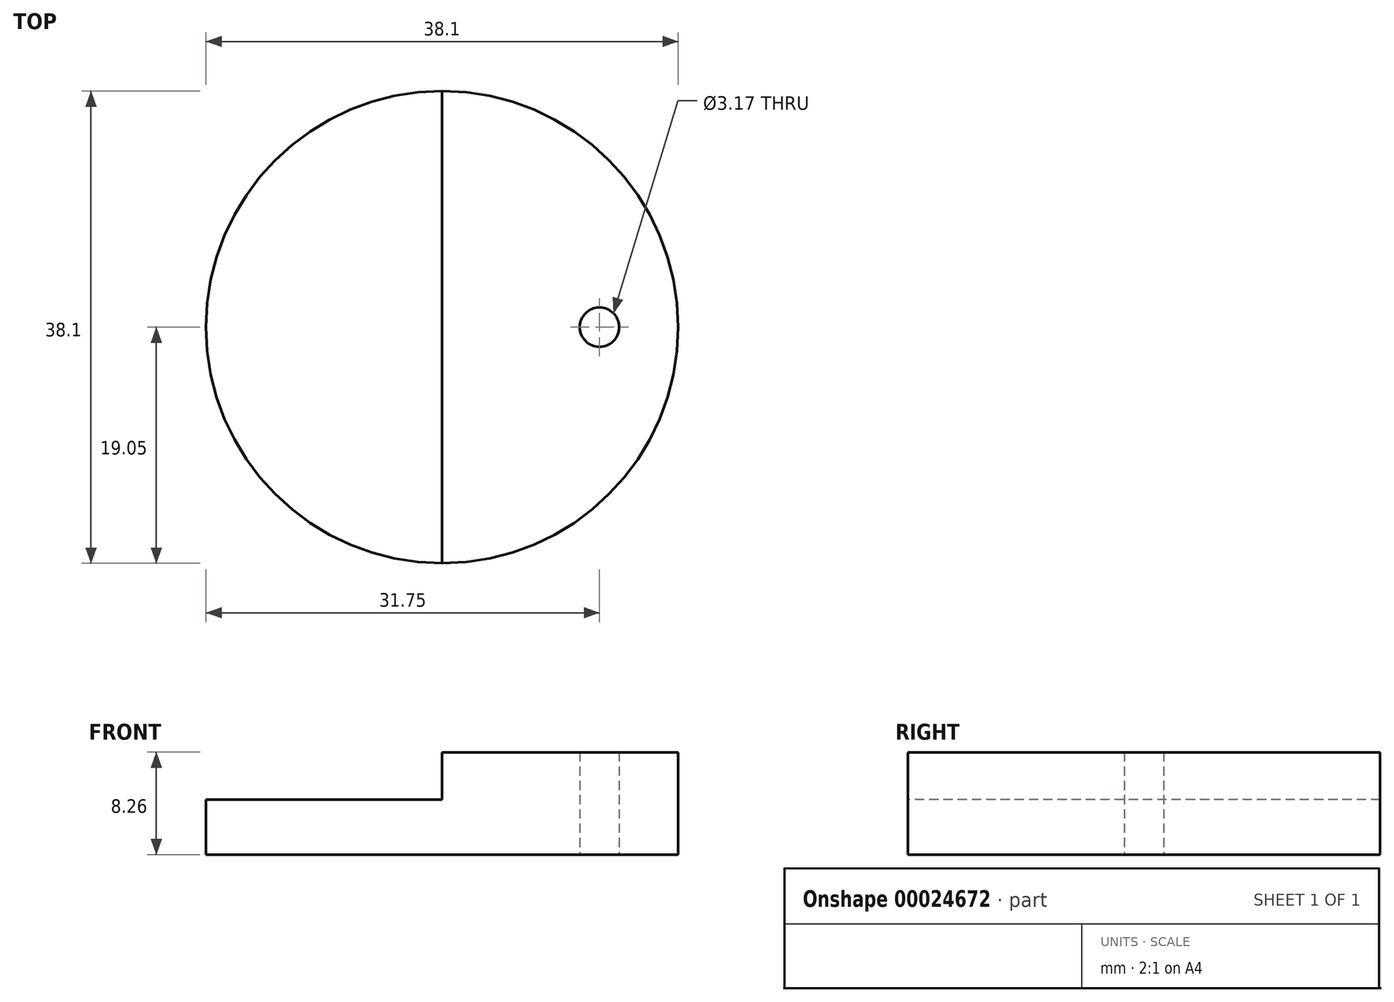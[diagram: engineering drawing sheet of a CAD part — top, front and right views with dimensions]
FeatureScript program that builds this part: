
annotation { "Feature Type Name" : "Feature", "Feature Type Description" : "" }
export const myFeature = defineFeature(function(context is Context, id is Id, definition is map)
    precondition{}
    {
        {
            var Q0;
            Q0=qCreatedBy(makeId("Top.planeOp"),FACE);
            var sketch = newSketch(context, id + "F0", { "sketchPlane" : qUnion([Q0])});
            skCircle(sketch, "E0", {"center": v(0, 0) * mm, "radius": 19.05 * mm});
            skCircle(sketch, "E1", {"center": v(12.7, 0) * mm, "radius": 1.59 * mm});
            skSolve(sketch);
        }
        {
            var Q0;
            Q0=makeQuery(id+"F0.imprint","IMPRINT",FACE,{"disambiguationData":[TD([[makeQuery(id+"F0.imprint","IMPRINT",EDGE,{"derivedFrom":sQuery(id+"F0.wireOp",EDGE,"E0")}),1.0]])]});
            extrude(context, id + "F1", {"entities" : qUnion([Q0]), "depth" : 8.25 * mm});
        }
        {
            var Q0;
            Q0=qCreatedBy(makeId("Top.planeOp"),FACE);
            var sketch = newSketch(context, id + "F2", { "sketchPlane" : qUnion([Q0])});
            skLineSegment(sketch, "E2.bottom", {"start": v(-36.06, 33.8) * mm, "end": v(0, 33.8) * mm});
            skLineSegment(sketch, "E2.top", {"start": v(-36.06, -31.55) * mm, "end": v(0, -31.55) * mm});
            skLineSegment(sketch, "E2.left", {"start": v(-36.06, 33.8) * mm, "end": v(-36.06, -31.55) * mm});
            skLineSegment(sketch, "E2.right", {"start": v(0, 33.8) * mm, "end": v(0, -31.55) * mm});
            skSolve(sketch);
        }
        {
            var Q0;
            Q0 = qSketchRegion(id + "F2", true);
            extrude(context, id + "F3", {"entities" : qUnion([Q0]), "operationType" : NewBodyOperationType.REMOVE, "depth" : 25.4 * mm, "hasSecondDirection" : true, "secondDirectionOppositeDirection" : false, "secondDirectionDepth" : 4.44 * mm});
        }
    });
